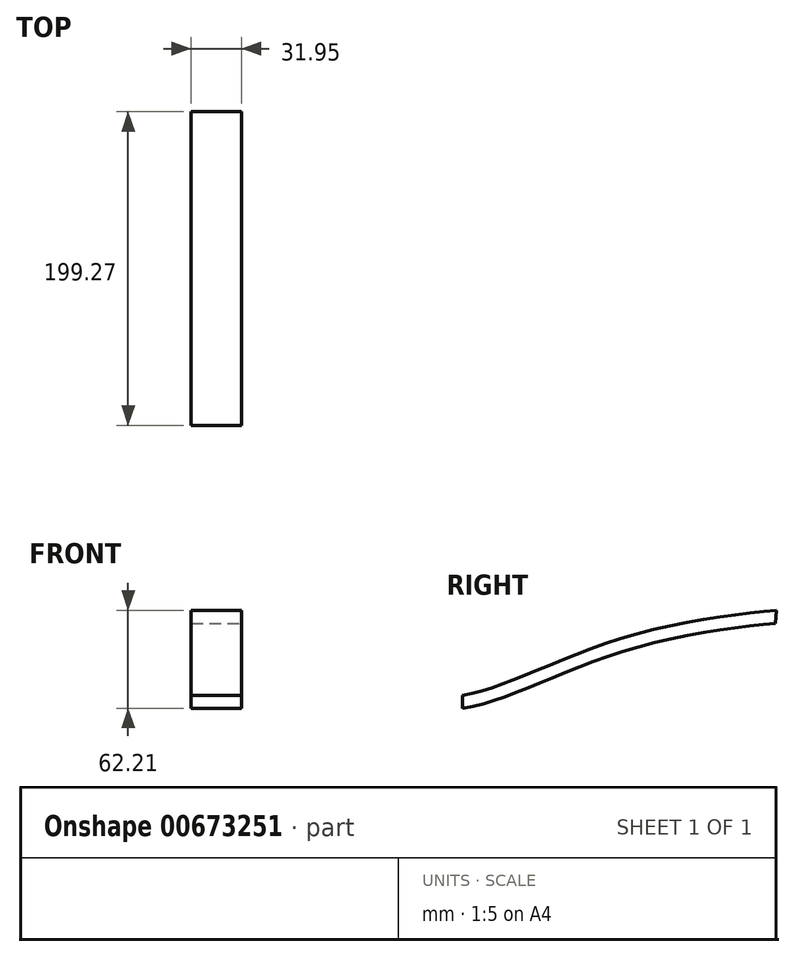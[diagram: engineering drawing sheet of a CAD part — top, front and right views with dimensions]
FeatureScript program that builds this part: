
annotation { "Feature Type Name" : "Feature", "Feature Type Description" : "" }
export const myFeature = defineFeature(function(context is Context, id is Id, definition is map)
    precondition{}
    {
        {
            var Q0;
            Q0=qCreatedBy(makeId("Right.planeOp"),FACE);
            var sketch = newSketch(context, id + "F0", { "sketchPlane" : qUnion([Q0])});
            skFitSpline(sketch, "E0", {"points": [v(0, 0) * mm, v(43.79, 13.84) * mm, v(117.55, 40.63) * mm, v(198.85, 53.94) * mm], "startDerivative": vector(155, 22.3) * mm, "endDerivative": vector(169.21, 15.62) * mm});
            skSolve(sketch);
        }
        {
            var Q0;
            Q0=qCreatedBy(makeId("Front.planeOp"),FACE);
            var sketch = newSketch(context, id + "F1", { "sketchPlane" : qUnion([Q0])});
            skLineSegment(sketch, "E1.bottom", {"start": v(-16.84, 0) * mm, "end": v(15.11, 0) * mm});
            skLineSegment(sketch, "E1.top", {"start": v(-16.84, 8.28) * mm, "end": v(15.11, 8.28) * mm});
            skLineSegment(sketch, "E1.left", {"start": v(-16.84, 0) * mm, "end": v(-16.84, 8.28) * mm});
            skLineSegment(sketch, "E1.right", {"start": v(15.11, 0) * mm, "end": v(15.11, 8.28) * mm});
            skSolve(sketch);
        }
        {
            var Q0;
            Q0 = qSketchRegion(id + "F1", true);
            var Q1;
            Q1 = qConstructionFilter(qBodyType(qCreatedBy(id + "F1" ,EDGE), BodyType.WIRE), ConstructionObject.NO);
            var Q2;
            Q2=sQuery(id+"F0.wireOp",EDGE,"E0");
            sweep(context, id + "F2", {"bodyType" : ToolBodyType.SURFACE, "profiles" : qUnion([Q0]), "surfaceProfiles" : qUnion([Q1]), "path" : qUnion([Q2])});
        }
    });
